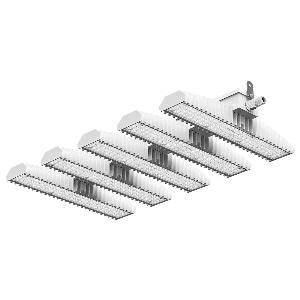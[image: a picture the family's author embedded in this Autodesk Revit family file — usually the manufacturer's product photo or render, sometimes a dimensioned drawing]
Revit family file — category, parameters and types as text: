
# Revit family: 3f_filippi_-_3f_lem_medio_3f_filippi_-_58915_-_3f_lem_5_led_250_dali_cr_medio
name_source: partatom
category: Lighting Fixtures
units: mm (PartAtom-declared; Revit-internal decimal feet)

## family parameters
Cut with Voids When Loaded = No
Host = Face
Light Source = No
Part Type = Normal
Room Calculation Point = No
Round Connector Dimension = Use Diameter
Shared = No

## types (1)
- 3F Filippi - 3F LEM Medio (1 x LED, 41574 lm, 274 W, 4000 K)
    Apparent Load = 274 VA
    Approval mark = CE
    CIE Flux Codes = 83 96 99 100 100
    Color Rendering = 80
    Color Temperature = 4000 K
    Control Gear = Electronic transformer
    Default Elevation = 1800 mm
    Description = Industrial luminaire with high light output and high luminous efficiency designed with the most innovative technologies for environments with temperature up to 55°C.

ILLUMINOTECHNICAL
Luminous efficiency 100% (DLOR 100%, ULOR 0%).
Initial luminous flux of the luminaire 41574 lm.
Medium distribution with rectangular shape.
Installation Interdistance Transv.D = 1.02 x hu - Long.D = 1.06 x hu.
Tabular UGR (CIE 117 - 4H-8H; S=0.25H; 70/50/20): RUG 19.2 - 18.8.
Beam angle: 65° - 67°.
Luminous efficacy 152 lm/W.
Lifetime (L93/B10): 30000 h. (tq+25°C)
Lifetime (L90/B10): 50000 h. (tq+25°C)
Lifetime (L85/B10): 80000 h. (tq+25°C)
Lifetime (L80/B10): 100000 h. (tq+25°C)
Lifetime (L85/B10): 50000 h. (tq+55°C)
Sudden decreased luminous flux after 50000 hours: 0% (C0).
Photobiological safety in compliance with IEC/TR 62778: RG0 risk exempt, (IEC 62471).
In compliance with IEC/EN 62722-2-1 - IEC/EN 62717 standards.

SOURCE
5 Mid-Power linear LED modules 50W/840.
Energy efficiency class (UE 2019/2020 - UE 2019/2015): C.
CIE 13.3 Colour rendering index: CRI >80 (R9 <50%).
IES TM-30 Fidelity Index: Rf = 84 Rg = 95.
CCT nominal colour temperature 4000 K.
Colour initial tolerance (MacAdam): SDCM 3.

MECHANICAL
Passive modular heatsinks in die-casted aluminium, painted in white colour.
To optimize the thermal management of the LED module, the heatsinks are oversized and provided with self-cleaning of cooling fins.
Wiring body in aluminium and galvanised steel anchored solidly to the sinks and thermally separated.
3F Lens lenses with high luminous efficiency, transparent methacrylate (PMMA), fixed to the LED modules.
Fixing brackets in stainless steel.
Luminaire with limited surface temperature. - D - (EN 60598-2-24)
Dimensions: 952x542 mm, height 129 mm. Weight 20.9 kg.
IP65 protection degree.
Mechanical strength to impacts IK06 (1 joule).
Glow-wire test resistance 650°C.

ELECTRICAL
Halogen Free DALI-2 DATI (Parts 251, 252, 253), PUSH-DIM, electronic wiring 230V-50/60Hz, power factor 0.97 at full load, THD <25%, constant output current, class I, 3 driver, 3 DALI addresses.
Power of the luminaire 274 W.
ENEC - CE.
SAFE FLICKER: PstLM=<1 and SVM=<0.4 (IEC TR 61547-1 and IEC TR 63158), to ensure a more comfortable and safe light.
Luminaire compliant with EN 60598-2-22 for power supply from a centralised emergency system CPSS (Central Power Supply System), not incorporated in the luminaire - high risk areas excluded. The default power and flux are 100% in AC and 15% in DC.
Ambient temperature from -30°C to +55°C.
Temperature class T6 max 85°C.
Quick connection via M25 5P connector with 9-13 mm tightening range.
Power unit positioned on a separate compartment by the LED module to ensure optimum temperatures of cabling components, to be inspectable and maintainable.
Relative humidity UR: <85%.

INSTALLATION
Ceiling / Suspended / Wall.
All accessories dedicated to this product are available on the Catalog and on our website www.3F-Filippi.com.

APPLICATIONS
In commercial environments, exhibition and industrial areas, stores, open areas.
Applications with high ambient temperature up to 55°C.
Environments in which it is necessary a total protection against falling fragments (eg environments with foodstuffs or machines with moving parts or with extreme temperature changes), use luminaires with polycarbonate lenses.

LIGHT MANAGEMENT
Recommended minimum setting: 10%.
The luminaire, equipped with (DALI-2 DATI) driver, can be controlled manually with 3F Easy Dim technology or automatically/manually with wired or wireless DALI/D2D control systems.
The D2D driver guarantees interoperability with other devices with the same certification by making the following information available:
Device Data (Part 251), Energy Report (Part 252), Diagnosis & Maintenance (Part 253).
In electrical systems without a regulation system (manual or automatic) and DALI bus, a suitable jumper must be made on the DA-DA terminals of the appliance.

WARNING
Fixture not suitable for cold stores with an ambient temperature <0°C and/or relative humidity >85%.
Luminaire designed for disposal/recycling at end-of-life.
Replaceable (LED only) light source by a professional. Replaceable control gear by a professional.
    Height = 129 mm
    Lamp = 1 x LED
    Lamp Light Flux = 41574 lm
    Lamp Power = 274 W
    Lamp count = 1
    Length = 952 mm
    Lifetime = 50000 h
    Luminous efficacy = 152 lm/W
    Manufacturer = 3F Filippi
    ModVariant = No
    Model = 3F Filippi - 58915 - 3F LEM 5 LED 250 DALI CR MEDIO
    Mounting Place = Ceiling
    Mounting Type = Pendant
    Number of Poles = 1
    OnlyDefault = Yes
    Power Factor = 1
    Product Name = 3F Filippi - 3F LEM Medio
    Product group = pendant luminaire
    ProductGroupID = 9
    Protection Class = Protection class I
    Protection Degree = IP 65
    RLX_Detail_Level = 1
    RLX_Emergency_Light_Flux = 0 lm
    RLX_Emergency_Type = 0
    RLX_Emergency_Type_DB = No
    RlxData = <blob elided: 134513 chars, md5=8e02fdaa>
    Socket = socket
    Standby Power = 0 W
    System Light Flux = 41574 lm
    System Power = 274 W
    Type Comments = Product without accessories
    Type Image = 3f_filippi_-_lem_5.jpg
    URL = http://relux.com
    VarID = ---
    Voltage = 0 V
    Weight = 0.00 kg
    Width = 542 mm

## geometry (parser evidence)
native form markers: Blend x4, Sweep x12
no freeform markers — native parametric forms only
